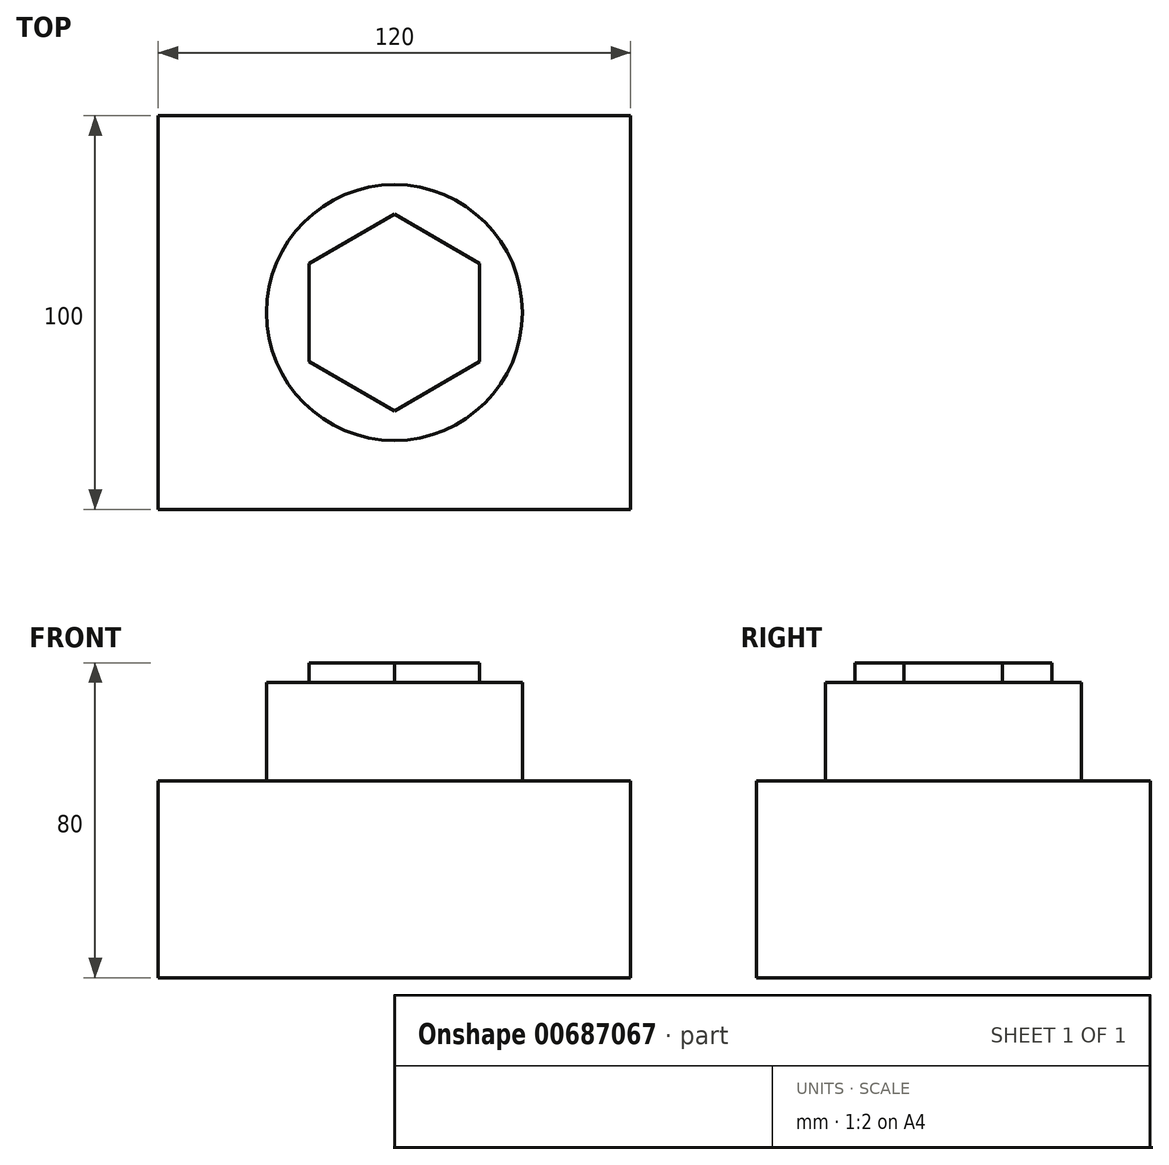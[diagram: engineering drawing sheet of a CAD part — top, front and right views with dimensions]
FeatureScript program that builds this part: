
annotation { "Feature Type Name" : "Feature", "Feature Type Description" : "" }
export const myFeature = defineFeature(function(context is Context, id is Id, definition is map)
    precondition{}
    {
        {
            var Q0;
            Q0=qCreatedBy(makeId("Top.planeOp"),FACE);
            var sketch = newSketch(context, id + "F0", { "sketchPlane" : qUnion([Q0])});
            skLineSegment(sketch, "E0.bottom", {"start": v(60, 50) * mm, "end": v(-60, 50) * mm});
            skLineSegment(sketch, "E0.top", {"start": v(60, -50) * mm, "end": v(-60, -50) * mm});
            skLineSegment(sketch, "E0.left", {"start": v(60, 50) * mm, "end": v(60, -50) * mm});
            skLineSegment(sketch, "E0.right", {"start": v(-60, 50) * mm, "end": v(-60, -50) * mm});
            skPoint(sketch, "E0.middle", {"position": v(0, 0) * mm});
            skSolve(sketch);
        }
        {
            var Q0;
            Q0 = qSketchRegion(id + "F0", true);
            extrude(context, id + "F1", {"entities" : qUnion([Q0]), "depth" : 50 * mm, "offsetDistance" : 25 * mm});
        }
        {
            var Q0;
            Q0=makeQuery(id+"F1.opExtrude","CAP_FACE",FACE,{"disambiguationData":[OSD([sQuery(id+"F0.wireOp",EDGE,"E0.bottom"),sQuery(id+"F0.wireOp",EDGE,"E0.top"),sQuery(id+"F0.wireOp",EDGE,"E0.left"),sQuery(id+"F0.wireOp",EDGE,"E0.right")])],"isStart":false});
            var sketch = newSketch(context, id + "F2", { "sketchPlane" : qUnion([Q0])});
            skCircle(sketch, "E1", {"center": v(0, 0) * mm, "radius": 32.5 * mm});
            skSolve(sketch);
        }
        {
            var Q0;
            Q0 = qSketchRegion(id + "F2", true);
            extrude(context, id + "F3", {"entities" : qUnion([Q0]), "operationType" : NewBodyOperationType.ADD, "depth" : 25 * mm, "offsetDistance" : 25 * mm});
        }
        {
            var Q0;
            Q0=makeQuery(id+"F3.opExtrude","CAP_FACE",FACE,{"disambiguationData":[OSD([sQuery(id+"F2.wireOp",EDGE,"E1")])],"isStart":false});
            var sketch = newSketch(context, id + "F4", { "sketchPlane" : qUnion([Q0])});
            skCircle(sketch, "E2.cCircle", {"center": v(0, 0) * mm, "radius": 21.65 * mm, "construction": true});
            skLineSegment(sketch, "E2.0", {"start": v(0, -25) * mm, "end": v(-21.65, -12.5) * mm});
            skLineSegment(sketch, "E2.1", {"start": v(-21.65, -12.5) * mm, "end": v(-21.65, 12.5) * mm});
            skLineSegment(sketch, "E2.2", {"start": v(-21.65, 12.5) * mm, "end": v(0, 25) * mm});
            skLineSegment(sketch, "E2.3", {"start": v(0, 25) * mm, "end": v(21.65, 12.5) * mm});
            skLineSegment(sketch, "E2.4", {"start": v(21.65, 12.5) * mm, "end": v(21.65, -12.5) * mm});
            skLineSegment(sketch, "E2.5", {"start": v(21.65, -12.5) * mm, "end": v(0, -25) * mm});
            skPoint(sketch, "E2.0.midPoint", {"position": v(-10.83, -18.75) * mm});
            skSolve(sketch);
        }
        {
            var Q0;
            Q0 = qSketchRegion(id + "F4", true);
            extrude(context, id + "F5", {"entities" : qUnion([Q0]), "operationType" : NewBodyOperationType.ADD, "depth" : 5 * mm, "offsetDistance" : 25 * mm});
        }
    });
